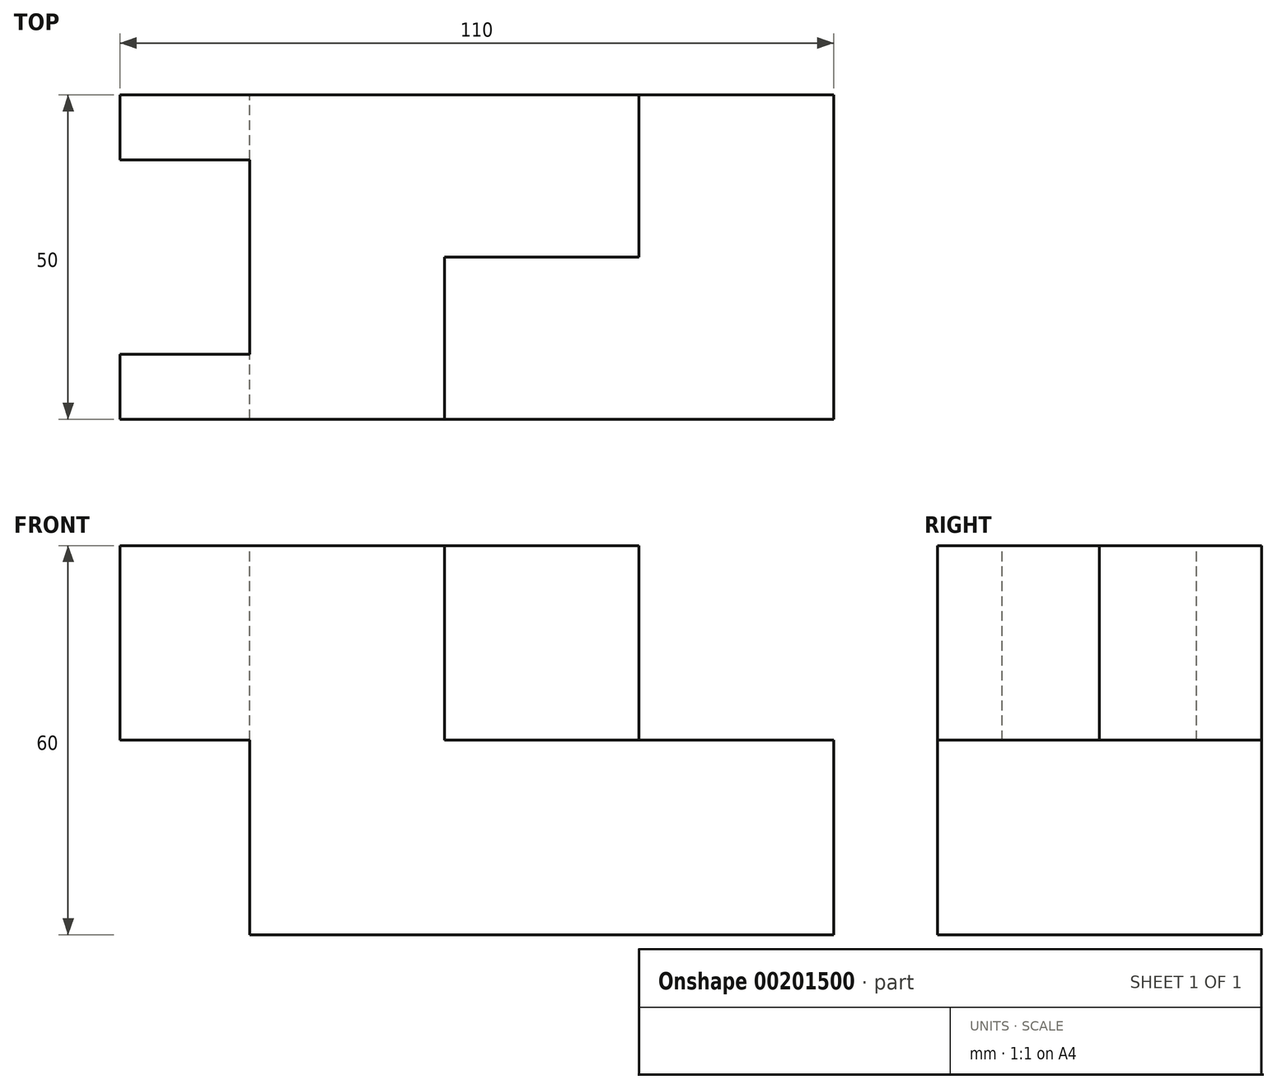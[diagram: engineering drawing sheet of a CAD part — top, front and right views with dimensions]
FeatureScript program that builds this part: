
annotation { "Feature Type Name" : "Feature", "Feature Type Description" : "" }
export const myFeature = defineFeature(function(context is Context, id is Id, definition is map)
    precondition{}
    {
        {
            var Q0;
            Q0=qCreatedBy(makeId("Front.planeOp"),FACE);
            var sketch = newSketch(context, id + "F0", { "sketchPlane" : qUnion([Q0])});
            skLineSegment(sketch, "E0", {"start": v(0, 0) * mm, "end": v(-90, 0) * mm});
            skLineSegment(sketch, "E1", {"start": v(-90, 0) * mm, "end": v(-90, 30) * mm});
            skLineSegment(sketch, "E2", {"start": v(-90, 30) * mm, "end": v(-110, 30) * mm});
            skLineSegment(sketch, "E3", {"start": v(-110, 30) * mm, "end": v(-110, 60) * mm});
            skLineSegment(sketch, "E4", {"start": v(-110, 60) * mm, "end": v(-30, 60) * mm});
            skLineSegment(sketch, "E5", {"start": v(-30, 60) * mm, "end": v(-30, 30) * mm});
            skLineSegment(sketch, "E6", {"start": v(-30, 30) * mm, "end": v(0, 30) * mm});
            skLineSegment(sketch, "E7", {"start": v(0, 30) * mm, "end": v(0, 0) * mm});
            skLineSegment(sketch, "E8", {"start": v(-90, 30) * mm, "end": v(-90, 60) * mm});
            skLineSegment(sketch, "E9", {"start": v(-30, 30) * mm, "end": v(-60, 30) * mm});
            skLineSegment(sketch, "E10", {"start": v(-60, 30) * mm, "end": v(-60, 60) * mm});
            skSolve(sketch);
        }
        {
            var Q0;
            Q0=qSketchRegion(id+"F0",true);
            extrude(context, id + "F1", {"entities" : qUnion([Q0]), "endBound" : BoundingType.SYMMETRIC, "depth" : 50 * mm});
        }
        {
            var Q0;
            Q0=makeQuery(id+"F0.imprint","IMPRINT",FACE,{"disambiguationData":[TD([[makeQuery(id+"F0.imprint","IMPRINT",EDGE,{"derivedFrom":sQuery(id+"F0.wireOp",EDGE,"E2")}),-1.0]])]});
            extrude(context, id + "F2", {"entities" : qUnion([Q0]), "operationType" : NewBodyOperationType.REMOVE, "endBound" : BoundingType.SYMMETRIC, "oppositeDirection" : true, "depth" : 30 * mm});
        }
        {
            var Q0;
            {var subQ0=sQuery(id+"F0.wireOp",EDGE,"E5");Q0=makeQuery(id+"F0.imprint","IMPRINT",FACE,{"disambiguationData":[TD([[makeQuery(id+"F0.imprint","IMPRINT",EDGE,{"derivedFrom":subQ0}),-1.0]])]});}
            extrude(context, id + "F3", {"entities" : qUnion([Q0]), "operationType" : NewBodyOperationType.REMOVE, "endBound" : BoundingType.THROUGH_ALL, "depth" : 25 * mm});
        }
    });
